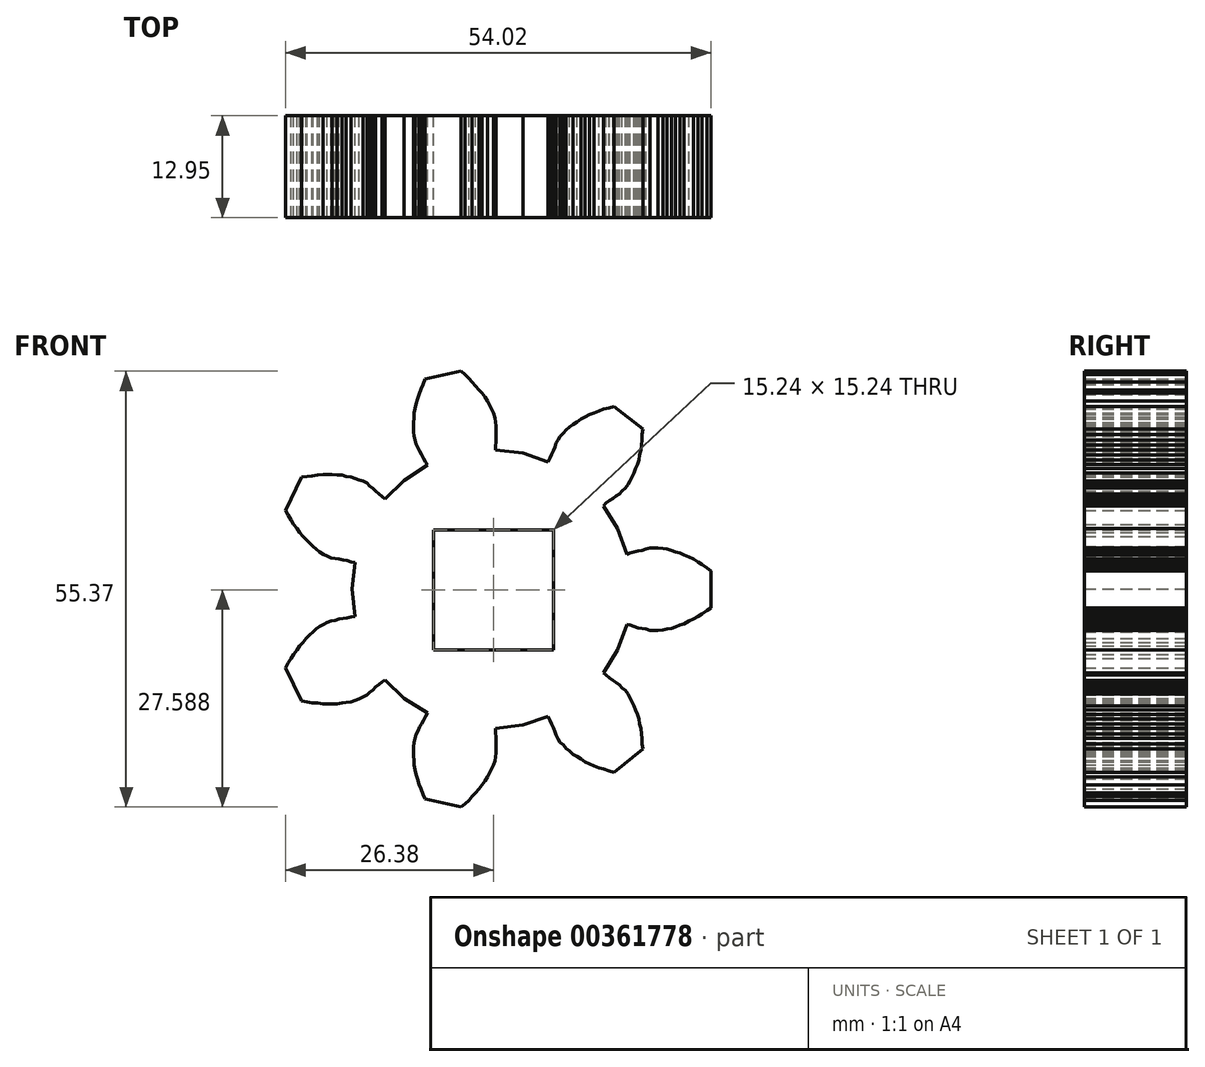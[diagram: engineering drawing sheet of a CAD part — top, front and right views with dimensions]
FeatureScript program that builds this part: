
annotation { "Feature Type Name" : "Feature", "Feature Type Description" : "" }
export const myFeature = defineFeature(function(context is Context, id is Id, definition is map)
    precondition{}
    {
        {
            var Q0;
            Q0=qCreatedBy(makeId("Front.planeOp"),FACE);
            var sketch = newSketch(context, id + "F0", { "sketchPlane" : qUnion([Q0])});
            skLineSegment(sketch, "E0", {"start": v(15.83, 18.2) * mm, "end": v(17.02, 21.42) * mm});
            skLineSegment(sketch, "E1", {"start": v(17.02, 21.42) * mm, "end": v(17.44, 21.34) * mm});
            skLineSegment(sketch, "E2", {"start": v(17.44, 21.34) * mm, "end": v(17.95, 21.17) * mm});
            skLineSegment(sketch, "E3", {"start": v(17.95, 21.17) * mm, "end": v(18.46, 21) * mm});
            skLineSegment(sketch, "E4", {"start": v(18.46, 21) * mm, "end": v(18.97, 20.91) * mm});
            skLineSegment(sketch, "E5", {"start": v(18.97, 20.91) * mm, "end": v(19.47, 20.83) * mm});
            skLineSegment(sketch, "E6", {"start": v(19.47, 20.83) * mm, "end": v(19.98, 20.66) * mm});
            skLineSegment(sketch, "E7", {"start": v(19.98, 20.66) * mm, "end": v(20.49, 20.66) * mm});
            skLineSegment(sketch, "E8", {"start": v(20.49, 20.66) * mm, "end": v(21, 20.66) * mm});
            skLineSegment(sketch, "E9", {"start": v(21, 20.66) * mm, "end": v(21.6, 20.74) * mm});
            skLineSegment(sketch, "E10", {"start": v(21.6, 20.74) * mm, "end": v(22.1, 20.83) * mm});
            skLineSegment(sketch, "E11", {"start": v(22.1, 20.83) * mm, "end": v(22.69, 20.91) * mm});
            skLineSegment(sketch, "E12", {"start": v(22.69, 20.91) * mm, "end": v(23.2, 21.08) * mm});
            skLineSegment(sketch, "E13", {"start": v(23.2, 21.08) * mm, "end": v(23.8, 21.34) * mm});
            skLineSegment(sketch, "E14", {"start": v(23.8, 21.34) * mm, "end": v(24.3, 21.5) * mm});
            skLineSegment(sketch, "E15", {"start": v(24.3, 21.5) * mm, "end": v(24.9, 21.84) * mm});
            skLineSegment(sketch, "E16", {"start": v(24.9, 21.84) * mm, "end": v(25.48, 22.1) * mm});
            skLineSegment(sketch, "E17", {"start": v(25.48, 22.1) * mm, "end": v(26.08, 22.44) * mm});
            skLineSegment(sketch, "E18", {"start": v(26.08, 22.44) * mm, "end": v(26.59, 22.78) * mm});
            skLineSegment(sketch, "E19", {"start": v(26.59, 22.78) * mm, "end": v(27.18, 23.2) * mm});
            skLineSegment(sketch, "E20", {"start": v(27.18, 23.2) * mm, "end": v(27.69, 23.54) * mm});
            skLineSegment(sketch, "E21", {"start": v(27.69, 23.54) * mm, "end": v(27.69, 28.2) * mm});
            skLineSegment(sketch, "E22", {"start": v(27.69, 28.2) * mm, "end": v(27.18, 28.62) * mm});
            skLineSegment(sketch, "E23", {"start": v(27.18, 28.62) * mm, "end": v(26.59, 29.04) * mm});
            skLineSegment(sketch, "E24", {"start": v(26.59, 29.04) * mm, "end": v(26.08, 29.38) * mm});
            skLineSegment(sketch, "E25", {"start": v(26.08, 29.38) * mm, "end": v(25.48, 29.72) * mm});
            skLineSegment(sketch, "E26", {"start": v(25.48, 29.72) * mm, "end": v(24.9, 29.97) * mm});
            skLineSegment(sketch, "E27", {"start": v(24.9, 29.97) * mm, "end": v(24.3, 30.23) * mm});
            skLineSegment(sketch, "E28", {"start": v(24.3, 30.23) * mm, "end": v(23.8, 30.48) * mm});
            skLineSegment(sketch, "E29", {"start": v(23.8, 30.48) * mm, "end": v(23.2, 30.65) * mm});
            skLineSegment(sketch, "E30", {"start": v(23.2, 30.65) * mm, "end": v(22.69, 30.82) * mm});
            skLineSegment(sketch, "E31", {"start": v(22.69, 30.82) * mm, "end": v(22.1, 30.99) * mm});
            skLineSegment(sketch, "E32", {"start": v(22.1, 30.99) * mm, "end": v(21.6, 31.07) * mm});
            skLineSegment(sketch, "E33", {"start": v(21.6, 31.07) * mm, "end": v(21, 31.16) * mm});
            skLineSegment(sketch, "E34", {"start": v(21, 31.16) * mm, "end": v(20.49, 31.16) * mm});
            skLineSegment(sketch, "E35", {"start": v(20.49, 31.16) * mm, "end": v(19.98, 31.16) * mm});
            skLineSegment(sketch, "E36", {"start": v(19.98, 31.16) * mm, "end": v(19.47, 30.99) * mm});
            skLineSegment(sketch, "E37", {"start": v(19.47, 30.99) * mm, "end": v(18.97, 30.82) * mm});
            skLineSegment(sketch, "E38", {"start": v(18.97, 30.82) * mm, "end": v(18.46, 30.73) * mm});
            skLineSegment(sketch, "E39", {"start": v(18.46, 30.73) * mm, "end": v(17.95, 30.65) * mm});
            skLineSegment(sketch, "E40", {"start": v(17.95, 30.65) * mm, "end": v(17.44, 30.48) * mm});
            skLineSegment(sketch, "E41", {"start": v(17.44, 30.48) * mm, "end": v(17.02, 30.31) * mm});
            skLineSegment(sketch, "E42", {"start": v(17.02, 30.31) * mm, "end": v(15.83, 33.61) * mm});
            skLineSegment(sketch, "E43", {"start": v(15.83, 33.61) * mm, "end": v(14.06, 36.5) * mm});
            skLineSegment(sketch, "E44", {"start": v(14.06, 36.5) * mm, "end": v(14.4, 36.83) * mm});
            skLineSegment(sketch, "E45", {"start": v(14.4, 36.83) * mm, "end": v(14.82, 37.17) * mm});
            skLineSegment(sketch, "E46", {"start": v(14.82, 37.17) * mm, "end": v(15.24, 37.42) * mm});
            skLineSegment(sketch, "E47", {"start": v(15.24, 37.42) * mm, "end": v(15.66, 37.76) * mm});
            skLineSegment(sketch, "E48", {"start": v(15.66, 37.76) * mm, "end": v(16.09, 38.02) * mm});
            skLineSegment(sketch, "E49", {"start": v(16.09, 38.02) * mm, "end": v(16.43, 38.35) * mm});
            skLineSegment(sketch, "E50", {"start": v(16.43, 38.35) * mm, "end": v(16.85, 38.78) * mm});
            skLineSegment(sketch, "E51", {"start": v(16.85, 38.78) * mm, "end": v(17.19, 39.2) * mm});
            skLineSegment(sketch, "E52", {"start": v(17.19, 39.2) * mm, "end": v(17.44, 39.62) * mm});
            skLineSegment(sketch, "E53", {"start": v(17.44, 39.62) * mm, "end": v(17.7, 40.13) * mm});
            skLineSegment(sketch, "E54", {"start": v(17.7, 40.13) * mm, "end": v(17.95, 40.64) * mm});
            skLineSegment(sketch, "E55", {"start": v(17.95, 40.64) * mm, "end": v(18.12, 41.23) * mm});
            skLineSegment(sketch, "E56", {"start": v(18.12, 41.23) * mm, "end": v(18.37, 41.74) * mm});
            skLineSegment(sketch, "E57", {"start": v(18.37, 41.74) * mm, "end": v(18.54, 42.33) * mm});
            skLineSegment(sketch, "E58", {"start": v(18.54, 42.33) * mm, "end": v(18.63, 42.93) * mm});
            skLineSegment(sketch, "E59", {"start": v(18.63, 42.93) * mm, "end": v(18.8, 43.6) * mm});
            skLineSegment(sketch, "E60", {"start": v(18.8, 43.6) * mm, "end": v(18.88, 44.2) * mm});
            skLineSegment(sketch, "E61", {"start": v(18.88, 44.2) * mm, "end": v(18.97, 44.87) * mm});
            skLineSegment(sketch, "E62", {"start": v(18.97, 44.87) * mm, "end": v(18.97, 45.55) * mm});
            skLineSegment(sketch, "E63", {"start": v(18.97, 45.55) * mm, "end": v(19.05, 46.23) * mm});
            skLineSegment(sketch, "E64", {"start": v(19.05, 46.23) * mm, "end": v(15.4, 49.1) * mm});
            skLineSegment(sketch, "E65", {"start": v(15.4, 49.1) * mm, "end": v(14.73, 48.94) * mm});
            skLineSegment(sketch, "E66", {"start": v(14.73, 48.94) * mm, "end": v(14.06, 48.77) * mm});
            skLineSegment(sketch, "E67", {"start": v(14.06, 48.77) * mm, "end": v(13.46, 48.51) * mm});
            skLineSegment(sketch, "E68", {"start": v(13.46, 48.51) * mm, "end": v(12.87, 48.26) * mm});
            skLineSegment(sketch, "E69", {"start": v(12.87, 48.26) * mm, "end": v(12.28, 48.1) * mm});
            skLineSegment(sketch, "E70", {"start": v(12.28, 48.1) * mm, "end": v(11.68, 47.75) * mm});
            skLineSegment(sketch, "E71", {"start": v(11.68, 47.75) * mm, "end": v(11.18, 47.5) * mm});
            skLineSegment(sketch, "E72", {"start": v(11.18, 47.5) * mm, "end": v(10.67, 47.16) * mm});
            skLineSegment(sketch, "E73", {"start": v(10.67, 47.16) * mm, "end": v(10.16, 46.82) * mm});
            skLineSegment(sketch, "E74", {"start": v(10.16, 46.82) * mm, "end": v(9.74, 46.48) * mm});
            skLineSegment(sketch, "E75", {"start": v(9.74, 46.48) * mm, "end": v(9.31, 46.14) * mm});
            skLineSegment(sketch, "E76", {"start": v(9.31, 46.14) * mm, "end": v(8.97, 45.72) * mm});
            skLineSegment(sketch, "E77", {"start": v(8.97, 45.72) * mm, "end": v(8.55, 45.3) * mm});
            skLineSegment(sketch, "E78", {"start": v(8.55, 45.3) * mm, "end": v(8.3, 44.87) * mm});
            skLineSegment(sketch, "E79", {"start": v(8.3, 44.87) * mm, "end": v(8.04, 44.45) * mm});
            skLineSegment(sketch, "E80", {"start": v(8.04, 44.45) * mm, "end": v(7.87, 43.94) * mm});
            skLineSegment(sketch, "E81", {"start": v(7.87, 43.94) * mm, "end": v(7.7, 43.52) * mm});
            skLineSegment(sketch, "E82", {"start": v(7.7, 43.52) * mm, "end": v(7.45, 43.01) * mm});
            skLineSegment(sketch, "E83", {"start": v(7.45, 43.01) * mm, "end": v(7.28, 42.59) * mm});
            skLineSegment(sketch, "E84", {"start": v(7.28, 42.59) * mm, "end": v(7.03, 42.08) * mm});
            skLineSegment(sketch, "E85", {"start": v(7.03, 42.08) * mm, "end": v(3.8, 43.18) * mm});
            skLineSegment(sketch, "E86", {"start": v(3.8, 43.18) * mm, "end": v(0.34, 43.6) * mm});
            skLineSegment(sketch, "E87", {"start": v(0.34, 43.6) * mm, "end": v(0.34, 44.11) * mm});
            skLineSegment(sketch, "E88", {"start": v(0.34, 44.11) * mm, "end": v(0.42, 44.62) * mm});
            skLineSegment(sketch, "E89", {"start": v(0.42, 44.62) * mm, "end": v(0.42, 45.13) * mm});
            skLineSegment(sketch, "E90", {"start": v(0.42, 45.13) * mm, "end": v(0.42, 45.64) * mm});
            skLineSegment(sketch, "E91", {"start": v(0.42, 45.64) * mm, "end": v(0.42, 46.14) * mm});
            skLineSegment(sketch, "E92", {"start": v(0.42, 46.14) * mm, "end": v(0.42, 46.65) * mm});
            skLineSegment(sketch, "E93", {"start": v(0.42, 46.65) * mm, "end": v(0.34, 47.16) * mm});
            skLineSegment(sketch, "E94", {"start": v(0.34, 47.16) * mm, "end": v(0.25, 47.67) * mm});
            skLineSegment(sketch, "E95", {"start": v(0.25, 47.67) * mm, "end": v(0.08, 48.26) * mm});
            skLineSegment(sketch, "E96", {"start": v(0.08, 48.26) * mm, "end": v(-0.17, 48.77) * mm});
            skLineSegment(sketch, "E97", {"start": v(-0.17, 48.77) * mm, "end": v(-0.42, 49.28) * mm});
            skLineSegment(sketch, "E98", {"start": v(-0.42, 49.28) * mm, "end": v(-0.68, 49.78) * mm});
            skLineSegment(sketch, "E99", {"start": v(-0.68, 49.78) * mm, "end": v(-1.02, 50.3) * mm});
            skLineSegment(sketch, "E100", {"start": v(-1.02, 50.3) * mm, "end": v(-1.36, 50.8) * mm});
            skLineSegment(sketch, "E101", {"start": v(-1.36, 50.8) * mm, "end": v(-1.78, 51.22) * mm});
            skLineSegment(sketch, "E102", {"start": v(-1.78, 51.22) * mm, "end": v(-2.2, 51.73) * mm});
            skLineSegment(sketch, "E103", {"start": v(-2.2, 51.73) * mm, "end": v(-2.62, 52.24) * mm});
            skLineSegment(sketch, "E104", {"start": v(-2.62, 52.24) * mm, "end": v(-3.05, 52.66) * mm});
            skLineSegment(sketch, "E105", {"start": v(-3.05, 52.66) * mm, "end": v(-3.56, 53.17) * mm});
            skLineSegment(sketch, "E106", {"start": v(-3.56, 53.17) * mm, "end": v(-4.06, 53.6) * mm});
            skLineSegment(sketch, "E107", {"start": v(-4.06, 53.6) * mm, "end": v(-8.64, 52.58) * mm});
            skLineSegment(sketch, "E108", {"start": v(-8.64, 52.58) * mm, "end": v(-8.9, 51.9) * mm});
            skLineSegment(sketch, "E109", {"start": v(-8.9, 51.9) * mm, "end": v(-9.14, 51.3) * mm});
            skLineSegment(sketch, "E110", {"start": v(-9.14, 51.3) * mm, "end": v(-9.4, 50.63) * mm});
            skLineSegment(sketch, "E111", {"start": v(-9.4, 50.63) * mm, "end": v(-9.57, 50.04) * mm});
            skLineSegment(sketch, "E112", {"start": v(-9.57, 50.04) * mm, "end": v(-9.74, 49.44) * mm});
            skLineSegment(sketch, "E113", {"start": v(-9.74, 49.44) * mm, "end": v(-9.9, 48.85) * mm});
            skLineSegment(sketch, "E114", {"start": v(-9.9, 48.85) * mm, "end": v(-10, 48.26) * mm});
            skLineSegment(sketch, "E115", {"start": v(-10, 48.26) * mm, "end": v(-10, 47.67) * mm});
            skLineSegment(sketch, "E116", {"start": v(-10, 47.67) * mm, "end": v(-10.08, 47.07) * mm});
            skLineSegment(sketch, "E117", {"start": v(-10.08, 47.07) * mm, "end": v(-10.08, 46.48) * mm});
            skLineSegment(sketch, "E118", {"start": v(-10.08, 46.48) * mm, "end": v(-10.08, 45.89) * mm});
            skLineSegment(sketch, "E119", {"start": v(-10.08, 45.89) * mm, "end": v(-10, 45.38) * mm});
            skLineSegment(sketch, "E120", {"start": v(-10, 45.38) * mm, "end": v(-9.9, 44.87) * mm});
            skLineSegment(sketch, "E121", {"start": v(-9.9, 44.87) * mm, "end": v(-9.74, 44.37) * mm});
            skLineSegment(sketch, "E122", {"start": v(-9.74, 44.37) * mm, "end": v(-9.48, 43.86) * mm});
            skLineSegment(sketch, "E123", {"start": v(-9.48, 43.86) * mm, "end": v(-9.31, 43.43) * mm});
            skLineSegment(sketch, "E124", {"start": v(-9.31, 43.43) * mm, "end": v(-9.06, 43.01) * mm});
            skLineSegment(sketch, "E125", {"start": v(-9.06, 43.01) * mm, "end": v(-8.8, 42.5) * mm});
            skLineSegment(sketch, "E126", {"start": v(-8.8, 42.5) * mm, "end": v(-8.55, 42.08) * mm});
            skLineSegment(sketch, "E127", {"start": v(-8.55, 42.08) * mm, "end": v(-8.3, 41.66) * mm});
            skLineSegment(sketch, "E128", {"start": v(-8.3, 41.66) * mm, "end": v(-11.26, 39.7) * mm});
            skLineSegment(sketch, "E129", {"start": v(-11.26, 39.7) * mm, "end": v(-13.72, 37.34) * mm});
            skLineSegment(sketch, "E130", {"start": v(-13.72, 37.34) * mm, "end": v(-14.06, 37.68) * mm});
            skLineSegment(sketch, "E131", {"start": v(-14.06, 37.68) * mm, "end": v(-14.48, 38.02) * mm});
            skLineSegment(sketch, "E132", {"start": v(-14.48, 38.02) * mm, "end": v(-14.9, 38.35) * mm});
            skLineSegment(sketch, "E133", {"start": v(-14.9, 38.35) * mm, "end": v(-15.24, 38.7) * mm});
            skLineSegment(sketch, "E134", {"start": v(-15.24, 38.7) * mm, "end": v(-15.66, 39.03) * mm});
            skLineSegment(sketch, "E135", {"start": v(-15.66, 39.03) * mm, "end": v(-16, 39.37) * mm});
            skLineSegment(sketch, "E136", {"start": v(-16, 39.37) * mm, "end": v(-16.5, 39.62) * mm});
            skLineSegment(sketch, "E137", {"start": v(-16.5, 39.62) * mm, "end": v(-17.02, 39.8) * mm});
            skLineSegment(sketch, "E138", {"start": v(-17.02, 39.8) * mm, "end": v(-17.53, 39.96) * mm});
            skLineSegment(sketch, "E139", {"start": v(-17.53, 39.96) * mm, "end": v(-18.03, 40.13) * mm});
            skLineSegment(sketch, "E140", {"start": v(-18.03, 40.13) * mm, "end": v(-18.63, 40.22) * mm});
            skLineSegment(sketch, "E141", {"start": v(-18.63, 40.22) * mm, "end": v(-19.13, 40.39) * mm});
            skLineSegment(sketch, "E142", {"start": v(-19.13, 40.39) * mm, "end": v(-19.81, 40.39) * mm});
            skLineSegment(sketch, "E143", {"start": v(-19.81, 40.39) * mm, "end": v(-20.4, 40.47) * mm});
            skLineSegment(sketch, "E144", {"start": v(-20.4, 40.47) * mm, "end": v(-21, 40.47) * mm});
            skLineSegment(sketch, "E145", {"start": v(-21, 40.47) * mm, "end": v(-21.6, 40.47) * mm});
            skLineSegment(sketch, "E146", {"start": v(-21.6, 40.47) * mm, "end": v(-22.27, 40.39) * mm});
            skLineSegment(sketch, "E147", {"start": v(-22.27, 40.39) * mm, "end": v(-22.95, 40.3) * mm});
            skLineSegment(sketch, "E148", {"start": v(-22.95, 40.3) * mm, "end": v(-23.62, 40.22) * mm});
            skLineSegment(sketch, "E149", {"start": v(-23.62, 40.22) * mm, "end": v(-24.3, 40.13) * mm});
            skLineSegment(sketch, "E150", {"start": v(-24.3, 40.13) * mm, "end": v(-26.33, 35.9) * mm});
            skLineSegment(sketch, "E151", {"start": v(-26.33, 35.9) * mm, "end": v(-26, 35.3) * mm});
            skLineSegment(sketch, "E152", {"start": v(-26, 35.3) * mm, "end": v(-25.65, 34.71) * mm});
            skLineSegment(sketch, "E153", {"start": v(-25.65, 34.71) * mm, "end": v(-25.32, 34.12) * mm});
            skLineSegment(sketch, "E154", {"start": v(-25.32, 34.12) * mm, "end": v(-24.9, 33.61) * mm});
            skLineSegment(sketch, "E155", {"start": v(-24.9, 33.61) * mm, "end": v(-24.55, 33.1) * mm});
            skLineSegment(sketch, "E156", {"start": v(-24.55, 33.1) * mm, "end": v(-24.13, 32.6) * mm});
            skLineSegment(sketch, "E157", {"start": v(-24.13, 32.6) * mm, "end": v(-23.7, 32.17) * mm});
            skLineSegment(sketch, "E158", {"start": v(-23.7, 32.17) * mm, "end": v(-23.28, 31.75) * mm});
            skLineSegment(sketch, "E159", {"start": v(-23.28, 31.75) * mm, "end": v(-22.86, 31.33) * mm});
            skLineSegment(sketch, "E160", {"start": v(-22.86, 31.33) * mm, "end": v(-22.44, 30.99) * mm});
            skLineSegment(sketch, "E161", {"start": v(-22.44, 30.99) * mm, "end": v(-22.01, 30.65) * mm});
            skLineSegment(sketch, "E162", {"start": v(-22.01, 30.65) * mm, "end": v(-21.5, 30.31) * mm});
            skLineSegment(sketch, "E163", {"start": v(-21.5, 30.31) * mm, "end": v(-21.08, 30.14) * mm});
            skLineSegment(sketch, "E164", {"start": v(-21.08, 30.14) * mm, "end": v(-20.57, 29.89) * mm});
            skLineSegment(sketch, "E165", {"start": v(-20.57, 29.89) * mm, "end": v(-20.07, 29.8) * mm});
            skLineSegment(sketch, "E166", {"start": v(-20.07, 29.8) * mm, "end": v(-19.56, 29.72) * mm});
            skLineSegment(sketch, "E167", {"start": v(-19.56, 29.72) * mm, "end": v(-19.05, 29.63) * mm});
            skLineSegment(sketch, "E168", {"start": v(-19.05, 29.63) * mm, "end": v(-18.54, 29.55) * mm});
            skLineSegment(sketch, "E169", {"start": v(-18.54, 29.55) * mm, "end": v(-18.03, 29.38) * mm});
            skLineSegment(sketch, "E170", {"start": v(-18.03, 29.38) * mm, "end": v(-17.53, 29.3) * mm});
            skLineSegment(sketch, "E171", {"start": v(-17.53, 29.3) * mm, "end": v(-17.86, 25.9) * mm});
            skLineSegment(sketch, "E172", {"start": v(-17.86, 25.9) * mm, "end": v(-17.53, 22.44) * mm});
            skLineSegment(sketch, "E173", {"start": v(-17.53, 22.44) * mm, "end": v(-18.03, 22.35) * mm});
            skLineSegment(sketch, "E174", {"start": v(-18.03, 22.35) * mm, "end": v(-18.54, 22.27) * mm});
            skLineSegment(sketch, "E175", {"start": v(-18.54, 22.27) * mm, "end": v(-19.05, 22.18) * mm});
            skLineSegment(sketch, "E176", {"start": v(-19.05, 22.18) * mm, "end": v(-19.56, 22.1) * mm});
            skLineSegment(sketch, "E177", {"start": v(-19.56, 22.1) * mm, "end": v(-20.07, 21.93) * mm});
            skLineSegment(sketch, "E178", {"start": v(-20.07, 21.93) * mm, "end": v(-20.57, 21.84) * mm});
            skLineSegment(sketch, "E179", {"start": v(-20.57, 21.84) * mm, "end": v(-21.08, 21.67) * mm});
            skLineSegment(sketch, "E180", {"start": v(-21.08, 21.67) * mm, "end": v(-21.5, 21.42) * mm});
            skLineSegment(sketch, "E181", {"start": v(-21.5, 21.42) * mm, "end": v(-22.01, 21.17) * mm});
            skLineSegment(sketch, "E182", {"start": v(-22.01, 21.17) * mm, "end": v(-22.44, 20.83) * mm});
            skLineSegment(sketch, "E183", {"start": v(-22.44, 20.83) * mm, "end": v(-22.86, 20.49) * mm});
            skLineSegment(sketch, "E184", {"start": v(-22.86, 20.49) * mm, "end": v(-23.28, 20.07) * mm});
            skLineSegment(sketch, "E185", {"start": v(-23.28, 20.07) * mm, "end": v(-23.7, 19.64) * mm});
            skLineSegment(sketch, "E186", {"start": v(-23.7, 19.64) * mm, "end": v(-24.13, 19.13) * mm});
            skLineSegment(sketch, "E187", {"start": v(-24.13, 19.13) * mm, "end": v(-24.55, 18.71) * mm});
            skLineSegment(sketch, "E188", {"start": v(-24.55, 18.71) * mm, "end": v(-24.9, 18.2) * mm});
            skLineSegment(sketch, "E189", {"start": v(-24.9, 18.2) * mm, "end": v(-25.32, 17.61) * mm});
            skLineSegment(sketch, "E190", {"start": v(-25.32, 17.61) * mm, "end": v(-25.65, 17.1) * mm});
            skLineSegment(sketch, "E191", {"start": v(-25.65, 17.1) * mm, "end": v(-26, 16.5) * mm});
            skLineSegment(sketch, "E192", {"start": v(-26, 16.5) * mm, "end": v(-26.33, 15.92) * mm});
            skLineSegment(sketch, "E193", {"start": v(-26.33, 15.92) * mm, "end": v(-24.3, 11.68) * mm});
            skLineSegment(sketch, "E194", {"start": v(-24.3, 11.68) * mm, "end": v(-23.62, 11.6) * mm});
            skLineSegment(sketch, "E195", {"start": v(-23.62, 11.6) * mm, "end": v(-22.95, 11.43) * mm});
            skLineSegment(sketch, "E196", {"start": v(-22.95, 11.43) * mm, "end": v(-22.27, 11.43) * mm});
            skLineSegment(sketch, "E197", {"start": v(-22.27, 11.43) * mm, "end": v(-21.6, 11.34) * mm});
            skLineSegment(sketch, "E198", {"start": v(-21.6, 11.34) * mm, "end": v(-21, 11.34) * mm});
            skLineSegment(sketch, "E199", {"start": v(-21, 11.34) * mm, "end": v(-20.4, 11.34) * mm});
            skLineSegment(sketch, "E200", {"start": v(-20.4, 11.34) * mm, "end": v(-19.81, 11.34) * mm});
            skLineSegment(sketch, "E201", {"start": v(-19.81, 11.34) * mm, "end": v(-19.13, 11.43) * mm});
            skLineSegment(sketch, "E202", {"start": v(-19.13, 11.43) * mm, "end": v(-18.63, 11.51) * mm});
            skLineSegment(sketch, "E203", {"start": v(-18.63, 11.51) * mm, "end": v(-18.03, 11.6) * mm});
            skLineSegment(sketch, "E204", {"start": v(-18.03, 11.6) * mm, "end": v(-17.53, 11.77) * mm});
            skLineSegment(sketch, "E205", {"start": v(-17.53, 11.77) * mm, "end": v(-17.02, 11.94) * mm});
            skLineSegment(sketch, "E206", {"start": v(-17.02, 11.94) * mm, "end": v(-16.5, 12.2) * mm});
            skLineSegment(sketch, "E207", {"start": v(-16.5, 12.2) * mm, "end": v(-16, 12.45) * mm});
            skLineSegment(sketch, "E208", {"start": v(-16, 12.45) * mm, "end": v(-15.66, 12.78) * mm});
            skLineSegment(sketch, "E209", {"start": v(-15.66, 12.78) * mm, "end": v(-15.24, 13.12) * mm});
            skLineSegment(sketch, "E210", {"start": v(-15.24, 13.12) * mm, "end": v(-14.9, 13.46) * mm});
            skLineSegment(sketch, "E211", {"start": v(-14.9, 13.46) * mm, "end": v(-14.48, 13.8) * mm});
            skLineSegment(sketch, "E212", {"start": v(-14.48, 13.8) * mm, "end": v(-14.06, 14.14) * mm});
            skLineSegment(sketch, "E213", {"start": v(-14.06, 14.14) * mm, "end": v(-13.72, 14.4) * mm});
            skLineSegment(sketch, "E214", {"start": v(-13.72, 14.4) * mm, "end": v(-11.26, 12.02) * mm});
            skLineSegment(sketch, "E215", {"start": v(-11.26, 12.02) * mm, "end": v(-8.3, 10.16) * mm});
            skLineSegment(sketch, "E216", {"start": v(-8.3, 10.16) * mm, "end": v(-8.55, 9.74) * mm});
            skLineSegment(sketch, "E217", {"start": v(-8.55, 9.74) * mm, "end": v(-8.8, 9.23) * mm});
            skLineSegment(sketch, "E218", {"start": v(-8.8, 9.23) * mm, "end": v(-9.06, 8.8) * mm});
            skLineSegment(sketch, "E219", {"start": v(-9.06, 8.8) * mm, "end": v(-9.31, 8.38) * mm});
            skLineSegment(sketch, "E220", {"start": v(-9.31, 8.38) * mm, "end": v(-9.48, 7.87) * mm});
            skLineSegment(sketch, "E221", {"start": v(-9.48, 7.87) * mm, "end": v(-9.74, 7.45) * mm});
            skLineSegment(sketch, "E222", {"start": v(-9.74, 7.45) * mm, "end": v(-9.9, 6.94) * mm});
            skLineSegment(sketch, "E223", {"start": v(-9.9, 6.94) * mm, "end": v(-10, 6.43) * mm});
            skLineSegment(sketch, "E224", {"start": v(-10, 6.43) * mm, "end": v(-10.08, 5.84) * mm});
            skLineSegment(sketch, "E225", {"start": v(-10.08, 5.84) * mm, "end": v(-10.08, 5.33) * mm});
            skLineSegment(sketch, "E226", {"start": v(-10.08, 5.33) * mm, "end": v(-10.08, 4.74) * mm});
            skLineSegment(sketch, "E227", {"start": v(-10.08, 4.74) * mm, "end": v(-10, 4.15) * mm});
            skLineSegment(sketch, "E228", {"start": v(-10, 4.15) * mm, "end": v(-10, 3.56) * mm});
            skLineSegment(sketch, "E229", {"start": v(-10, 3.56) * mm, "end": v(-9.9, 2.96) * mm});
            skLineSegment(sketch, "E230", {"start": v(-9.9, 2.96) * mm, "end": v(-9.74, 2.37) * mm});
            skLineSegment(sketch, "E231", {"start": v(-9.74, 2.37) * mm, "end": v(-9.57, 1.78) * mm});
            skLineSegment(sketch, "E232", {"start": v(-9.57, 1.78) * mm, "end": v(-9.4, 1.1) * mm});
            skLineSegment(sketch, "E233", {"start": v(-9.4, 1.1) * mm, "end": v(-9.14, 0.5) * mm});
            skLineSegment(sketch, "E234", {"start": v(-9.14, 0.5) * mm, "end": v(-8.9, -0.17) * mm});
            skLineSegment(sketch, "E235", {"start": v(-8.9, -0.17) * mm, "end": v(-8.64, -0.76) * mm});
            skLineSegment(sketch, "E236", {"start": v(-8.64, -0.76) * mm, "end": v(-4.06, -1.78) * mm});
            skLineSegment(sketch, "E237", {"start": v(-4.06, -1.78) * mm, "end": v(-3.56, -1.36) * mm});
            skLineSegment(sketch, "E238", {"start": v(-3.56, -1.36) * mm, "end": v(-3.05, -0.93) * mm});
            skLineSegment(sketch, "E239", {"start": v(-3.05, -0.93) * mm, "end": v(-2.62, -0.42) * mm});
            skLineSegment(sketch, "E240", {"start": v(-2.62, -0.42) * mm, "end": v(-2.2, 0) * mm});
            skLineSegment(sketch, "E241", {"start": v(-2.2, 0) * mm, "end": v(-1.78, 0.5) * mm});
            skLineSegment(sketch, "E242", {"start": v(-1.78, 0.5) * mm, "end": v(-1.36, 1.02) * mm});
            skLineSegment(sketch, "E243", {"start": v(-1.36, 1.02) * mm, "end": v(-1.02, 1.52) * mm});
            skLineSegment(sketch, "E244", {"start": v(-1.02, 1.52) * mm, "end": v(-0.68, 2.03) * mm});
            skLineSegment(sketch, "E245", {"start": v(-0.68, 2.03) * mm, "end": v(-0.42, 2.54) * mm});
            skLineSegment(sketch, "E246", {"start": v(-0.42, 2.54) * mm, "end": v(-0.17, 3.05) * mm});
            skLineSegment(sketch, "E247", {"start": v(-0.17, 3.05) * mm, "end": v(0.08, 3.56) * mm});
            skLineSegment(sketch, "E248", {"start": v(0.08, 3.56) * mm, "end": v(0.25, 4.06) * mm});
            skLineSegment(sketch, "E249", {"start": v(0.25, 4.06) * mm, "end": v(0.34, 4.57) * mm});
            skLineSegment(sketch, "E250", {"start": v(0.34, 4.57) * mm, "end": v(0.42, 5.08) * mm});
            skLineSegment(sketch, "E251", {"start": v(0.42, 5.08) * mm, "end": v(0.42, 5.59) * mm});
            skLineSegment(sketch, "E252", {"start": v(0.42, 5.59) * mm, "end": v(0.42, 6.1) * mm});
            skLineSegment(sketch, "E253", {"start": v(0.42, 6.1) * mm, "end": v(0.42, 6.6) * mm});
            skLineSegment(sketch, "E254", {"start": v(0.42, 6.6) * mm, "end": v(0.42, 7.11) * mm});
            skLineSegment(sketch, "E255", {"start": v(0.42, 7.11) * mm, "end": v(0.34, 7.62) * mm});
            skLineSegment(sketch, "E256", {"start": v(0.34, 7.62) * mm, "end": v(0.34, 8.21) * mm});
            skLineSegment(sketch, "E257", {"start": v(0.34, 8.21) * mm, "end": v(3.8, 8.64) * mm});
            skLineSegment(sketch, "E258", {"start": v(3.8, 8.64) * mm, "end": v(7.03, 9.74) * mm});
            skLineSegment(sketch, "E259", {"start": v(7.03, 9.74) * mm, "end": v(7.28, 9.23) * mm});
            skLineSegment(sketch, "E260", {"start": v(7.28, 9.23) * mm, "end": v(7.45, 8.8) * mm});
            skLineSegment(sketch, "E261", {"start": v(7.45, 8.8) * mm, "end": v(7.7, 8.3) * mm});
            skLineSegment(sketch, "E262", {"start": v(7.7, 8.3) * mm, "end": v(7.87, 7.79) * mm});
            skLineSegment(sketch, "E263", {"start": v(7.87, 7.79) * mm, "end": v(8.04, 7.37) * mm});
            skLineSegment(sketch, "E264", {"start": v(8.04, 7.37) * mm, "end": v(8.3, 6.86) * mm});
            skLineSegment(sketch, "E265", {"start": v(8.3, 6.86) * mm, "end": v(8.55, 6.43) * mm});
            skLineSegment(sketch, "E266", {"start": v(8.55, 6.43) * mm, "end": v(8.97, 6.1) * mm});
            skLineSegment(sketch, "E267", {"start": v(8.97, 6.1) * mm, "end": v(9.31, 5.67) * mm});
            skLineSegment(sketch, "E268", {"start": v(9.31, 5.67) * mm, "end": v(9.74, 5.33) * mm});
            skLineSegment(sketch, "E269", {"start": v(9.74, 5.33) * mm, "end": v(10.16, 4.91) * mm});
            skLineSegment(sketch, "E270", {"start": v(10.16, 4.91) * mm, "end": v(10.67, 4.66) * mm});
            skLineSegment(sketch, "E271", {"start": v(10.67, 4.66) * mm, "end": v(11.18, 4.32) * mm});
            skLineSegment(sketch, "E272", {"start": v(11.18, 4.32) * mm, "end": v(11.68, 3.98) * mm});
            skLineSegment(sketch, "E273", {"start": v(11.68, 3.98) * mm, "end": v(12.28, 3.73) * mm});
            skLineSegment(sketch, "E274", {"start": v(12.28, 3.73) * mm, "end": v(12.87, 3.47) * mm});
            skLineSegment(sketch, "E275", {"start": v(12.87, 3.47) * mm, "end": v(13.46, 3.22) * mm});
            skLineSegment(sketch, "E276", {"start": v(13.46, 3.22) * mm, "end": v(14.06, 3.05) * mm});
            skLineSegment(sketch, "E277", {"start": v(14.06, 3.05) * mm, "end": v(14.73, 2.8) * mm});
            skLineSegment(sketch, "E278", {"start": v(14.73, 2.8) * mm, "end": v(15.4, 2.62) * mm});
            skLineSegment(sketch, "E279", {"start": v(15.4, 2.62) * mm, "end": v(19.05, 5.59) * mm});
            skLineSegment(sketch, "E280", {"start": v(19.05, 5.59) * mm, "end": v(18.97, 6.27) * mm});
            skLineSegment(sketch, "E281", {"start": v(18.97, 6.27) * mm, "end": v(18.97, 6.94) * mm});
            skLineSegment(sketch, "E282", {"start": v(18.97, 6.94) * mm, "end": v(18.88, 7.54) * mm});
            skLineSegment(sketch, "E283", {"start": v(18.88, 7.54) * mm, "end": v(18.8, 8.21) * mm});
            skLineSegment(sketch, "E284", {"start": v(18.8, 8.21) * mm, "end": v(18.63, 8.8) * mm});
            skLineSegment(sketch, "E285", {"start": v(18.63, 8.8) * mm, "end": v(18.54, 9.4) * mm});
            skLineSegment(sketch, "E286", {"start": v(18.54, 9.4) * mm, "end": v(18.37, 10) * mm});
            skLineSegment(sketch, "E287", {"start": v(18.37, 10) * mm, "end": v(18.12, 10.58) * mm});
            skLineSegment(sketch, "E288", {"start": v(18.12, 10.58) * mm, "end": v(17.95, 11.1) * mm});
            skLineSegment(sketch, "E289", {"start": v(17.95, 11.1) * mm, "end": v(17.7, 11.6) * mm});
            skLineSegment(sketch, "E290", {"start": v(17.7, 11.6) * mm, "end": v(17.44, 12.1) * mm});
            skLineSegment(sketch, "E291", {"start": v(17.44, 12.1) * mm, "end": v(17.19, 12.62) * mm});
            skLineSegment(sketch, "E292", {"start": v(17.19, 12.62) * mm, "end": v(16.85, 13.04) * mm});
            skLineSegment(sketch, "E293", {"start": v(16.85, 13.04) * mm, "end": v(16.43, 13.38) * mm});
            skLineSegment(sketch, "E294", {"start": v(16.43, 13.38) * mm, "end": v(16.09, 13.72) * mm});
            skLineSegment(sketch, "E295", {"start": v(16.09, 13.72) * mm, "end": v(15.66, 14.06) * mm});
            skLineSegment(sketch, "E296", {"start": v(15.66, 14.06) * mm, "end": v(15.24, 14.3) * mm});
            skLineSegment(sketch, "E297", {"start": v(15.24, 14.3) * mm, "end": v(14.82, 14.65) * mm});
            skLineSegment(sketch, "E298", {"start": v(14.82, 14.65) * mm, "end": v(14.4, 14.99) * mm});
            skLineSegment(sketch, "E299", {"start": v(14.4, 14.99) * mm, "end": v(14.06, 15.24) * mm});
            skLineSegment(sketch, "E300", {"start": v(14.06, 15.24) * mm, "end": v(15.83, 18.2) * mm});
            skLineSegment(sketch, "E301", {"start": v(-7.57, 18.19) * mm, "end": v(7.67, 18.19) * mm});
            skLineSegment(sketch, "E302", {"start": v(7.67, 18.19) * mm, "end": v(7.67, 33.43) * mm});
            skLineSegment(sketch, "E303", {"start": v(7.67, 33.43) * mm, "end": v(-7.57, 33.43) * mm});
            skLineSegment(sketch, "E304", {"start": v(-7.57, 33.43) * mm, "end": v(-7.57, 18.19) * mm});
            skSolve(sketch);
        }
        {
            var Q0;
            Q0=makeQuery(id+"F0.imprint","IMPRINT",FACE,{"disambiguationData":[TD([[makeQuery(id+"F0.imprint","IMPRINT",EDGE,{"derivedFrom":sQuery(id+"F0.wireOp",EDGE,"E0")}),1.0]])]});
            extrude(context, id + "F1", {"entities" : qUnion([Q0]), "depth" : 12.95 * mm});
        }
    });
